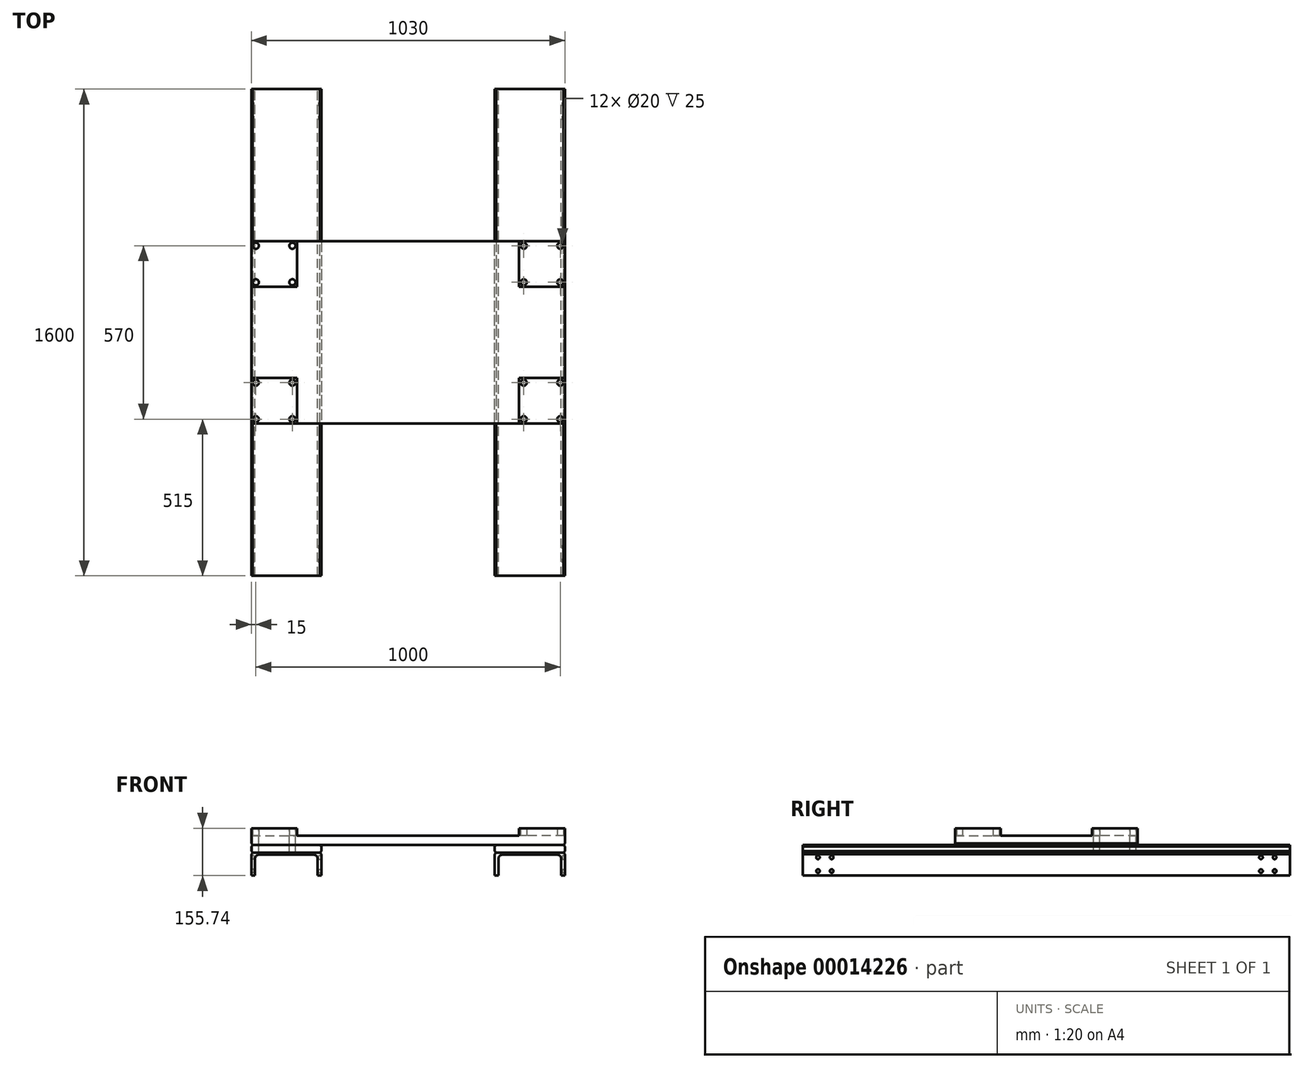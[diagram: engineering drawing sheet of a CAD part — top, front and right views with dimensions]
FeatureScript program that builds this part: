
annotation { "Feature Type Name" : "Feature", "Feature Type Description" : "" }
export const myFeature = defineFeature(function(context is Context, id is Id, definition is map)
    precondition{}
    {
        {
            var Q0;
            Q0=qCreatedBy(makeId("Front.planeOp"),FACE);
            var sketch = newSketch(context, id + "F0", { "sketchPlane" : qUnion([Q0])});
            skLineSegment(sketch, "E0", {"start": v(-285, 0) * mm, "end": v(-285, 75) * mm});
            skLineSegment(sketch, "E1", {"start": v(-285, 75) * mm, "end": v(-400, 75) * mm});
            skLineSegment(sketch, "E2", {"start": v(-285, 0) * mm, "end": v(-297.5, 0) * mm});
            skLineSegment(sketch, "E3", {"start": v(-297.5, 0) * mm, "end": v(-297.5, 56.5) * mm});
            skLineSegment(sketch, "E4", {"start": v(-309.5, 68.5) * mm, "end": v(-400, 68.5) * mm});
            skPoint(sketch, "E5.visualSharp", {"position": v(-297.5, 68.5) * mm});
            skArc(sketch, "E5.filletArc", {"start": v(-297.5, 56.5) * mm, "mid": v(-301.01, 64.99) * mm, "end": v(-309.5, 68.5) * mm});
            skPoint(sketch, "E6.0.MirrorP", {"position": v(-502.5, 68.5) * mm});
            skLineSegment(sketch, "E6.1.MirrorCS", {"start": v(-515, 0) * mm, "end": v(-515, 75) * mm});
            skLineSegment(sketch, "E6.2.MirrorCS", {"start": v(-502.5, 0) * mm, "end": v(-502.5, 56.5) * mm});
            skLineSegment(sketch, "E6.3.MirrorCS", {"start": v(-490.5, 68.5) * mm, "end": v(-400, 68.5) * mm});
            skLineSegment(sketch, "E6.4.MirrorCS", {"start": v(-515, 75) * mm, "end": v(-400, 75) * mm});
            skLineSegment(sketch, "E6.5.MirrorCS", {"start": v(-515, 0) * mm, "end": v(-502.5, 0) * mm});
            skArc(sketch, "E6.6.MirrorCS", {"start": v(-502.5, 56.5) * mm, "mid": v(-498.99, 64.99) * mm, "end": v(-490.5, 68.5) * mm});
            skSolve(sketch);
        }
        {
            var Q0;
            Q0=qSketchRegion(id+"F0",true);
            extrude(context, id + "F1", {"entities" : qUnion([Q0]), "depth" : 1600 * mm});
        }
        {
            var Q0;
            Q0=makeQuery(id+"F1.opExtrude","SWEPT_FACE",FACE,{"disambiguationData":[OSD([sQuery(id+"F0.wireOp",EDGE,"E0")])]});
            var sketch = newSketch(context, id + "F2", { "sketchPlane" : qUnion([Q0])});
            skLineSegment(sketch, "E7", {"start": v(-1600, 37.5) * mm, "end": v(0, 37.5) * mm, "construction": true});
            skLineSegment(sketch, "E8.rect.bottom", {"start": v(-1505, 15) * mm, "end": v(-1550, 15) * mm, "construction": true});
            skLineSegment(sketch, "E8.rect.top", {"start": v(-1505, 60) * mm, "end": v(-1550, 60) * mm, "construction": true});
            skLineSegment(sketch, "E8.rect.left", {"start": v(-1505, 15) * mm, "end": v(-1505, 60) * mm, "construction": true});
            skLineSegment(sketch, "E8.rect.right", {"start": v(-1550, 15) * mm, "end": v(-1550, 60) * mm, "construction": true});
            skPoint(sketch, "E8.rect.middle", {"position": v(-1527.5, 37.5) * mm});
            skCircle(sketch, "E9", {"center": v(-1550, 60) * mm, "radius": 6 * mm});
            skCircle(sketch, "E10", {"center": v(-1505, 60) * mm, "radius": 6 * mm});
            skCircle(sketch, "E11", {"center": v(-1550, 15) * mm, "radius": 6 * mm});
            skCircle(sketch, "E12", {"center": v(-1505, 15) * mm, "radius": 6 * mm});
            skLineSegment(sketch, "E13", {"start": v(-1527.5, 37.5) * mm, "end": v(-1527.5, 75) * mm, "construction": true});
            skLineSegment(sketch, "E14", {"start": v(-1527.5, 75) * mm, "end": v(-1527.5, 0) * mm, "construction": true});
            skLineSegment(sketch, "E15", {"start": v(-800, 75) * mm, "end": v(-800, 0) * mm, "construction": true});
            skLineSegment(sketch, "E16.0.MirrorCS", {"start": v(-72.5, 75) * mm, "end": v(-72.5, 0) * mm, "construction": true});
            skLineSegment(sketch, "E16.1.MirrorCS", {"start": v(-72.5, 37.5) * mm, "end": v(-72.5, 75) * mm, "construction": true});
            skCircle(sketch, "E16.2.MirrorC", {"center": v(-50, 60) * mm, "radius": 6 * mm});
            skCircle(sketch, "E16.3.MirrorC", {"center": v(-95, 60) * mm, "radius": 6 * mm});
            skLineSegment(sketch, "E16.4.MirrorCS", {"start": v(-95, 15) * mm, "end": v(-95, 60) * mm, "construction": true});
            skLineSegment(sketch, "E16.5.MirrorCS", {"start": v(-50, 15) * mm, "end": v(-50, 60) * mm, "construction": true});
            skLineSegment(sketch, "E16.6.MirrorCS", {"start": v(-95, 15) * mm, "end": v(-50, 15) * mm, "construction": true});
            skCircle(sketch, "E16.7.MirrorC", {"center": v(-95, 15) * mm, "radius": 6 * mm});
            skCircle(sketch, "E16.8.MirrorC", {"center": v(-50, 15) * mm, "radius": 6 * mm});
            skLineSegment(sketch, "E16.9.MirrorCS", {"start": v(-95, 60) * mm, "end": v(-50, 60) * mm, "construction": true});
            skPoint(sketch, "E16.10.MirrorP", {"position": v(-72.5, 37.5) * mm});
            skSolve(sketch);
        }
        {
            var Q0;
            Q0=qSketchRegion(id+"F2",true);
            extrude(context, id + "F3", {"entities" : qUnion([Q0]), "oppositeDirection" : true, "depth" : 8 * mm});
        }
        {
            var Q0;
            Q0=makeQuery(id+"F1.opExtrude","SWEPT_FACE",FACE,{"disambiguationData":[OSD([sQuery(id+"F0.wireOp",EDGE,"E6.1.MirrorCS")])]});
            var sketch = newSketch(context, id + "F4", { "sketchPlane" : qUnion([Q0])});
            skLineSegment(sketch, "E17", {"start": v(0, 37.5) * mm, "end": v(1600, 37.5) * mm, "construction": true});
            skLineSegment(sketch, "E18.rect.bottom", {"start": v(95, 15) * mm, "end": v(50, 15) * mm, "construction": true});
            skLineSegment(sketch, "E18.rect.top", {"start": v(95, 60) * mm, "end": v(50, 60) * mm, "construction": true});
            skLineSegment(sketch, "E18.rect.left", {"start": v(95, 15) * mm, "end": v(95, 60) * mm, "construction": true});
            skLineSegment(sketch, "E18.rect.right", {"start": v(50, 15) * mm, "end": v(50, 60) * mm, "construction": true});
            skPoint(sketch, "E18.rect.middle", {"position": v(72.5, 37.5) * mm});
            skCircle(sketch, "E19", {"center": v(50, 60) * mm, "radius": 6 * mm});
            skCircle(sketch, "E20", {"center": v(95, 60) * mm, "radius": 6 * mm});
            skCircle(sketch, "E21", {"center": v(50, 15) * mm, "radius": 6 * mm});
            skCircle(sketch, "E22", {"center": v(95, 15) * mm, "radius": 6 * mm});
            skLineSegment(sketch, "E23", {"start": v(72.5, 37.5) * mm, "end": v(72.5, 75) * mm, "construction": true});
            skLineSegment(sketch, "E24", {"start": v(72.5, 75) * mm, "end": v(72.5, 0) * mm, "construction": true});
            skLineSegment(sketch, "E25", {"start": v(800, 75) * mm, "end": v(800, 0) * mm, "construction": true});
            skLineSegment(sketch, "E26.0.MirrorCS", {"start": v(1527.5, 75) * mm, "end": v(1527.5, 0) * mm, "construction": true});
            skLineSegment(sketch, "E26.1.MirrorCS", {"start": v(1527.5, 37.5) * mm, "end": v(1527.5, 75) * mm, "construction": true});
            skCircle(sketch, "E26.2.MirrorC", {"center": v(1550, 60) * mm, "radius": 6 * mm});
            skCircle(sketch, "E26.3.MirrorC", {"center": v(1505, 60) * mm, "radius": 6 * mm});
            skLineSegment(sketch, "E26.4.MirrorCS", {"start": v(1505, 15) * mm, "end": v(1505, 60) * mm, "construction": true});
            skLineSegment(sketch, "E26.5.MirrorCS", {"start": v(1550, 15) * mm, "end": v(1550, 60) * mm, "construction": true});
            skLineSegment(sketch, "E26.6.MirrorCS", {"start": v(1505, 15) * mm, "end": v(1550, 15) * mm, "construction": true});
            skCircle(sketch, "E26.7.MirrorC", {"center": v(1505, 15) * mm, "radius": 6 * mm});
            skCircle(sketch, "E26.8.MirrorC", {"center": v(1550, 15) * mm, "radius": 6 * mm});
            skLineSegment(sketch, "E26.9.MirrorCS", {"start": v(1505, 60) * mm, "end": v(1550, 60) * mm, "construction": true});
            skPoint(sketch, "E26.10.MirrorP", {"position": v(1527.5, 37.5) * mm});
            skLineSegment(sketch, "E27", {"start": v(0, 75) * mm, "end": v(1600, 0) * mm, "construction": true});
            skLineSegment(sketch, "E28", {"start": v(1600, 0) * mm, "end": v(1600, 75) * mm, "construction": true});
            skLineSegment(sketch, "E29", {"start": v(1600, 75) * mm, "end": v(0, 0) * mm, "construction": true});
            skLineSegment(sketch, "E30", {"start": v(0, 0) * mm, "end": v(0, 75) * mm, "construction": true});
            skPoint(sketch, "E31", {"position": v(800, 37.5) * mm});
            skPoint(sketch, "E32", {"position": v(1600, 37.5) * mm});
            skPoint(sketch, "E33", {"position": v(0, 37.5) * mm});
            skSolve(sketch);
        }
        {
            var Q0;
            Q0=qSketchRegion(id+"F4",true);
            extrude(context, id + "F5", {"entities" : qUnion([Q0]), "operationType" : NewBodyOperationType.REMOVE, "oppositeDirection" : true, "depth" : 8 * mm});
        }
        {
            var Q0;
            Q0=makeQuery(id+"F1.opExtrude","SWEPT_FACE",FACE,{"disambiguationData":[OSD([sQuery(id+"F0.wireOp",EDGE,"E1"),sQuery(id+"F0.wireOp",EDGE,"E6.4.MirrorCS")])]});
            var sketch = newSketch(context, id + "F6", { "sketchPlane" : qUnion([Q0])});
            skLineSegment(sketch, "E34.bottom", {"start": v(-515, 0) * mm, "end": v(-285, 0) * mm});
            skLineSegment(sketch, "E34.top", {"start": v(-515, -1600) * mm, "end": v(-285, -1600) * mm});
            skLineSegment(sketch, "E34.left", {"start": v(-515, 0) * mm, "end": v(-515, -1600) * mm});
            skLineSegment(sketch, "E34.right", {"start": v(-285, 0) * mm, "end": v(-285, -1600) * mm});
            skSolve(sketch);
        }
        {
            var Q0;
            Q0=qSketchRegion(id+"F6",true);
            extrude(context, id + "F7", {"entities" : qUnion([Q0]), "depth" : 25.74 * mm});
        }
        {
            var Q0;
            Q0=makeQuery(id+"F1.opExtrude","SWEPT_BODY",BODY,{"disambiguationData":[OSD([sQuery(id+"F0.wireOp",EDGE,"E0"),sQuery(id+"F0.wireOp",EDGE,"E1"),sQuery(id+"F0.wireOp",EDGE,"E2"),sQuery(id+"F0.wireOp",EDGE,"E3"),sQuery(id+"F0.wireOp",EDGE,"E4"),sQuery(id+"F0.wireOp",EDGE,"E5.filletArc"),sQuery(id+"F0.wireOp",EDGE,"E6.1.MirrorCS"),sQuery(id+"F0.wireOp",EDGE,"E6.2.MirrorCS"),sQuery(id+"F0.wireOp",EDGE,"E6.3.MirrorCS"),sQuery(id+"F0.wireOp",EDGE,"E6.4.MirrorCS"),sQuery(id+"F0.wireOp",EDGE,"E6.5.MirrorCS"),sQuery(id+"F0.wireOp",EDGE,"E6.6.MirrorCS")])]});
            var Q1;
            Q1=makeQuery(id+"F7.opExtrude","SWEPT_BODY",BODY,{"disambiguationData":[OSD([sQuery(id+"F6.wireOp",EDGE,"E34.bottom"),sQuery(id+"F6.wireOp",EDGE,"E34.top"),sQuery(id+"F6.wireOp",EDGE,"E34.left"),sQuery(id+"F6.wireOp",EDGE,"E34.right")])]});
            var Q2;
            Q2=qCreatedBy(makeId("Right.planeOp"),FACE);
            mirror(context, id + "F8", {"entities" : qUnion([Q0, Q1]), "mirrorPlane" : qUnion([Q2])});
        }
        {
            var Q0;
            Q0=makeQuery(id+"F7.opExtrude","CAP_FACE",FACE,{"disambiguationData":[OSD([sQuery(id+"F6.wireOp",EDGE,"E34.bottom"),sQuery(id+"F6.wireOp",EDGE,"E34.top"),sQuery(id+"F6.wireOp",EDGE,"E34.left"),sQuery(id+"F6.wireOp",EDGE,"E34.right")])],"isStart":false});
            var sketch = newSketch(context, id + "F9", { "sketchPlane" : qUnion([Q0])});
            skLineSegment(sketch, "E35", {"start": v(-515, -800) * mm, "end": v(515, -800) * mm, "construction": true});
            skLineSegment(sketch, "E36", {"start": v(-515, -800) * mm, "end": v(-515, -500) * mm});
            skLineSegment(sketch, "E37", {"start": v(-515, -500) * mm, "end": v(515, -500) * mm});
            skLineSegment(sketch, "E38", {"start": v(515, -500) * mm, "end": v(515, -800) * mm});
            skLineSegment(sketch, "E39.0.MirrorCS", {"start": v(-515, -800) * mm, "end": v(-515, -1100) * mm});
            skLineSegment(sketch, "E39.1.MirrorCS", {"start": v(-515, -1100) * mm, "end": v(515, -1100) * mm});
            skLineSegment(sketch, "E39.2.MirrorCS", {"start": v(515, -1100) * mm, "end": v(515, -800) * mm});
            skSolve(sketch);
        }
        {
            var Q0;
            Q0=qSketchRegion(id+"F9",true);
            extrude(context, id + "F10", {"entities" : qUnion([Q0]), "depth" : 30 * mm});
        }
        {
            var Q0;
            Q0=makeQuery(id+"F8.opPattern","COPY",EDGE,{"derivedFrom":makeQuery(id+"F7.opExtrude","CAP_EDGE",EDGE,{"disambiguationData":[OSD([sQuery(id+"F6.wireOp",EDGE,"E34.left")])],"isStart":false}),"instanceName":"1"});
            var Q1;
            Q1=makeQuery(id+"F8.opPattern","COPY",EDGE,{"derivedFrom":makeQuery(id+"F7.opExtrude","CAP_EDGE",EDGE,{"disambiguationData":[OSD([sQuery(id+"F6.wireOp",EDGE,"E34.right")])],"isStart":false}),"instanceName":"1"});
            var Q2;
            Q2=makeQuery(id+"F7.opExtrude","CAP_EDGE",EDGE,{"disambiguationData":[OSD([sQuery(id+"F6.wireOp",EDGE,"E34.right")])],"isStart":false});
            var Q3;
            Q3=makeQuery(id+"F7.opExtrude","CAP_EDGE",EDGE,{"disambiguationData":[OSD([sQuery(id+"F6.wireOp",EDGE,"E34.left")])],"isStart":false});
            var Q4;
            Q4=makeQuery(id+"F1.opExtrude","SWEPT_EDGE",EDGE,{"disambiguationData":[OSD([sQuery(id+"F0.wireOp",EDGE,"E0"),sQuery(id+"F0.wireOp",EDGE,"E1")])]});
            var Q5;
            Q5=makeQuery(id+"F1.opExtrude","SWEPT_EDGE",EDGE,{"disambiguationData":[OSD([sQuery(id+"F0.wireOp",EDGE,"E6.1.MirrorCS"),sQuery(id+"F0.wireOp",EDGE,"E6.4.MirrorCS")])]});
            var Q6;
            Q6=makeQuery(id+"F8.opPattern","COPY",EDGE,{"derivedFrom":makeQuery(id+"F1.opExtrude","SWEPT_EDGE",EDGE,{"disambiguationData":[OSD([sQuery(id+"F0.wireOp",EDGE,"E6.1.MirrorCS"),sQuery(id+"F0.wireOp",EDGE,"E6.4.MirrorCS")])]}),"instanceName":"1"});
            var Q7;
            Q7=makeQuery(id+"F8.opPattern","COPY",EDGE,{"derivedFrom":makeQuery(id+"F1.opExtrude","SWEPT_EDGE",EDGE,{"disambiguationData":[OSD([sQuery(id+"F0.wireOp",EDGE,"E0"),sQuery(id+"F0.wireOp",EDGE,"E1")])]}),"instanceName":"1"});
            chamfer(context, id + "F11", {"entities" : qUnion([Q0, Q1, Q2, Q3, Q4, Q5, Q6, Q7]), "width" : 5 * mm, "tangentPropagation" : true});
        }
        {
            var Q0;
            Q0=makeQuery(id+"F7.opExtrude","CAP_EDGE",EDGE,{"disambiguationData":[OSD([sQuery(id+"F6.wireOp",EDGE,"E34.right")])],"isStart":true});
            var Q1;
            Q1=makeQuery(id+"F7.opExtrude","CAP_EDGE",EDGE,{"disambiguationData":[OSD([sQuery(id+"F6.wireOp",EDGE,"E34.left")])],"isStart":true});
            var Q2;
            Q2=makeQuery(id+"F8.opPattern","COPY",EDGE,{"derivedFrom":makeQuery(id+"F7.opExtrude","CAP_EDGE",EDGE,{"disambiguationData":[OSD([sQuery(id+"F6.wireOp",EDGE,"E34.right")])],"isStart":true}),"instanceName":"1"});
            var Q3;
            Q3=makeQuery(id+"F8.opPattern","COPY",EDGE,{"derivedFrom":makeQuery(id+"F7.opExtrude","CAP_EDGE",EDGE,{"disambiguationData":[OSD([sQuery(id+"F6.wireOp",EDGE,"E34.left")])],"isStart":true}),"instanceName":"1"});
            var Q4;
            Q4=makeQuery(id+"F10.opExtrude","CAP_EDGE",EDGE,{"disambiguationData":[OSD([sQuery(id+"F9.wireOp",EDGE,"E38"),sQuery(id+"F9.wireOp",EDGE,"E39.2.MirrorCS")])],"isStart":true});
            var Q5;
            Q5=makeQuery(id+"F10.opExtrude","CAP_EDGE",EDGE,{"disambiguationData":[OSD([sQuery(id+"F9.wireOp",EDGE,"E36"),sQuery(id+"F9.wireOp",EDGE,"E39.0.MirrorCS")])],"isStart":true});
            chamfer(context, id + "F12", {"entities" : qUnion([Q0, Q1, Q2, Q3, Q4, Q5]), "width" : 5 * mm, "tangentPropagation" : true});
        }
        {
            var Q0;
            Q0=makeQuery(id+"F10.opExtrude","CAP_FACE",FACE,{"disambiguationData":[OSD([sQuery(id+"F9.wireOp",EDGE,"E36"),sQuery(id+"F9.wireOp",EDGE,"E37"),sQuery(id+"F9.wireOp",EDGE,"E38"),sQuery(id+"F9.wireOp",EDGE,"E39.0.MirrorCS"),sQuery(id+"F9.wireOp",EDGE,"E39.1.MirrorCS"),sQuery(id+"F9.wireOp",EDGE,"E39.2.MirrorCS")])],"isStart":false});
            var sketch = newSketch(context, id + "F13", { "sketchPlane" : qUnion([Q0])});
            skLineSegment(sketch, "E40", {"start": v(0, -500) * mm, "end": v(0, -1100) * mm});
            skLineSegment(sketch, "E41", {"start": v(0, -800) * mm, "end": v(-515, -800) * mm});
            skLineSegment(sketch, "E42.rect.bottom", {"start": v(-515, -500) * mm, "end": v(-365, -500) * mm});
            skLineSegment(sketch, "E42.rect.top", {"start": v(-515, -650) * mm, "end": v(-365, -650) * mm});
            skLineSegment(sketch, "E42.rect.left", {"start": v(-515, -500) * mm, "end": v(-515, -650) * mm});
            skLineSegment(sketch, "E42.rect.right", {"start": v(-365, -500) * mm, "end": v(-365, -650) * mm});
            skPoint(sketch, "E42.rect.middle", {"position": v(-440, -575) * mm});
            skCircle(sketch, "E43", {"center": v(-500, -515) * mm, "radius": 10 * mm});
            skCircle(sketch, "E44", {"center": v(-380, -515) * mm, "radius": 10 * mm});
            skCircle(sketch, "E45", {"center": v(-380, -635) * mm, "radius": 10 * mm});
            skCircle(sketch, "E46", {"center": v(-500, -635) * mm, "radius": 10 * mm});
            skLineSegment(sketch, "E47", {"start": v(-440, -575) * mm, "end": v(-440, -500) * mm, "construction": true});
            skLineSegment(sketch, "E48", {"start": v(-440, -500) * mm, "end": v(-440, -650) * mm, "construction": true});
            skLineSegment(sketch, "E49.0.MirrorCS", {"start": v(0, -800) * mm, "end": v(515, -800) * mm});
            skLineSegment(sketch, "E50.0.MirrorCS", {"start": v(-440, -1025) * mm, "end": v(-440, -1100) * mm, "construction": true});
            skCircle(sketch, "E50.3.MirrorC", {"center": v(-380, -1085) * mm, "radius": 10 * mm});
            skCircle(sketch, "E50.4.MirrorC", {"center": v(-500, -1085) * mm, "radius": 10 * mm});
            skCircle(sketch, "E50.6.MirrorC", {"center": v(-500, -965) * mm, "radius": 10 * mm});
            skPoint(sketch, "E50.7.MirrorP", {"position": v(-440, -1025) * mm});
            skLineSegment(sketch, "E50.12.MirrorCS", {"start": v(-440, -1100) * mm, "end": v(-440, -950) * mm, "construction": true});
            skLineSegment(sketch, "E50.16.MirrorCS", {"start": v(-515, -950) * mm, "end": v(-365, -950) * mm});
            skLineSegment(sketch, "E50.17.MirrorCS", {"start": v(-365, -1100) * mm, "end": v(-365, -950) * mm});
            skCircle(sketch, "E50.18.MirrorC", {"center": v(-380, -965) * mm, "radius": 10 * mm});
            skPoint(sketch, "E50.19.MirrorP", {"position": v(-440, -1025) * mm});
            skLineSegment(sketch, "E50.20.MirrorCS", {"start": v(-515, -1100) * mm, "end": v(-365, -1100) * mm});
            skLineSegment(sketch, "E50.23.MirrorCS", {"start": v(-515, -1100) * mm, "end": v(-515, -950) * mm});
            skLineSegment(sketch, "E51.0.MirrorCS", {"start": v(440, -575) * mm, "end": v(440, -500) * mm, "construction": true});
            skCircle(sketch, "E51.1.MirrorC", {"center": v(500, -965) * mm, "radius": 10 * mm});
            skCircle(sketch, "E51.2.MirrorC", {"center": v(500, -635) * mm, "radius": 10 * mm});
            skCircle(sketch, "E51.3.MirrorC", {"center": v(380, -1085) * mm, "radius": 10 * mm});
            skCircle(sketch, "E51.4.MirrorC", {"center": v(380, -965) * mm, "radius": 10 * mm});
            skCircle(sketch, "E51.5.MirrorC", {"center": v(500, -1085) * mm, "radius": 10 * mm});
            skCircle(sketch, "E51.6.MirrorC", {"center": v(380, -515) * mm, "radius": 10 * mm});
            skCircle(sketch, "E51.7.MirrorC", {"center": v(380, -635) * mm, "radius": 10 * mm});
            skCircle(sketch, "E51.8.MirrorC", {"center": v(500, -515) * mm, "radius": 10 * mm});
            skLineSegment(sketch, "E51.9.MirrorCS", {"start": v(515, -1100) * mm, "end": v(365, -1100) * mm});
            skLineSegment(sketch, "E51.10.MirrorCS", {"start": v(440, -500) * mm, "end": v(440, -650) * mm, "construction": true});
            skLineSegment(sketch, "E51.11.MirrorCS", {"start": v(515, -950) * mm, "end": v(365, -950) * mm});
            skPoint(sketch, "E51.12.MirrorP", {"position": v(440, -575) * mm});
            skLineSegment(sketch, "E51.13.MirrorCS", {"start": v(515, -1100) * mm, "end": v(515, -950) * mm});
            skPoint(sketch, "E51.14.MirrorP", {"position": v(440, -1025) * mm});
            skLineSegment(sketch, "E51.15.MirrorCS", {"start": v(515, -500) * mm, "end": v(515, -650) * mm});
            skPoint(sketch, "E51.16.MirrorP", {"position": v(440, -1025) * mm});
            skLineSegment(sketch, "E51.17.MirrorCS", {"start": v(440, -1025) * mm, "end": v(440, -1100) * mm, "construction": true});
            skLineSegment(sketch, "E51.18.MirrorCS", {"start": v(440, -1100) * mm, "end": v(440, -950) * mm, "construction": true});
            skLineSegment(sketch, "E51.19.MirrorCS", {"start": v(515, -650) * mm, "end": v(365, -650) * mm});
            skLineSegment(sketch, "E51.20.MirrorCS", {"start": v(515, -500) * mm, "end": v(365, -500) * mm});
            skLineSegment(sketch, "E51.21.MirrorCS", {"start": v(365, -1100) * mm, "end": v(365, -950) * mm});
            skLineSegment(sketch, "E51.22.MirrorCS", {"start": v(365, -500) * mm, "end": v(365, -650) * mm});
            skPoint(sketch, "E51.23.MirrorP", {"position": v(440, -575) * mm});
            skSolve(sketch);
        }
        {
            var Q0;
            Q0=makeQuery(id+"F13.imprint","IMPRINT",FACE,{"disambiguationData":[TD([[makeQuery(id+"F13.imprint","IMPRINT",EDGE,{"derivedFrom":sQuery(id+"F13.wireOp",EDGE,"E43")}),1.0]])]});
            var Q1;
            Q1=makeQuery(id+"F13.imprint","IMPRINT",FACE,{"disambiguationData":[TD([[makeQuery(id+"F13.imprint","IMPRINT",EDGE,{"derivedFrom":sQuery(id+"F13.wireOp",EDGE,"E44")}),1.0]])]});
            var Q2;
            Q2=makeQuery(id+"F13.imprint","IMPRINT",FACE,{"disambiguationData":[TD([[makeQuery(id+"F13.imprint","IMPRINT",EDGE,{"derivedFrom":sQuery(id+"F13.wireOp",EDGE,"E46")}),1.0]])]});
            var Q3;
            Q3=makeQuery(id+"F13.imprint","IMPRINT",FACE,{"disambiguationData":[TD([[makeQuery(id+"F13.imprint","IMPRINT",EDGE,{"derivedFrom":sQuery(id+"F13.wireOp",EDGE,"E45")}),1.0]])]});
            var Q4;
            Q4=makeQuery(id+"F1.opExtrude","SWEPT_BODY",BODY,{"disambiguationData":[OSD([sQuery(id+"F0.wireOp",EDGE,"E0"),sQuery(id+"F0.wireOp",EDGE,"E1"),sQuery(id+"F0.wireOp",EDGE,"E2"),sQuery(id+"F0.wireOp",EDGE,"E3"),sQuery(id+"F0.wireOp",EDGE,"E4"),sQuery(id+"F0.wireOp",EDGE,"E5.filletArc"),sQuery(id+"F0.wireOp",EDGE,"E6.1.MirrorCS"),sQuery(id+"F0.wireOp",EDGE,"E6.2.MirrorCS"),sQuery(id+"F0.wireOp",EDGE,"E6.3.MirrorCS"),sQuery(id+"F0.wireOp",EDGE,"E6.4.MirrorCS"),sQuery(id+"F0.wireOp",EDGE,"E6.5.MirrorCS"),sQuery(id+"F0.wireOp",EDGE,"E6.6.MirrorCS")])]});
            extrude(context, id + "F14", {"entities" : qUnion([Q0, Q1, Q2, Q3]), "operationType" : NewBodyOperationType.REMOVE, "endBound" : BoundingType.UP_TO_BODY, "oppositeDirection" : true, "endBoundEntityBody" : qUnion([Q4]), "depth" : 25 * mm});
        }
        {
            var Q0;
            Q0=qSketchRegion(id+"F13",true);
            extrude(context, id + "F15", {"entities" : qUnion([Q0]), "operationType" : NewBodyOperationType.ADD, "depth" : 25 * mm});
        }
        {
            var Q0;
            Q0=makeQuery(id+"F13.imprint","IMPRINT",FACE,{"disambiguationData":[TD([[makeQuery(id+"F13.imprint","IMPRINT",EDGE,{"derivedFrom":sQuery(id+"F13.wireOp",EDGE,"E43")}),1.0]])]});
            var Q1;
            Q1=makeQuery(id+"F13.imprint","IMPRINT",FACE,{"disambiguationData":[TD([[makeQuery(id+"F13.imprint","IMPRINT",EDGE,{"derivedFrom":sQuery(id+"F13.wireOp",EDGE,"E46")}),1.0]])]});
            var Q2;
            Q2=makeQuery(id+"F13.imprint","IMPRINT",FACE,{"disambiguationData":[TD([[makeQuery(id+"F13.imprint","IMPRINT",EDGE,{"derivedFrom":sQuery(id+"F13.wireOp",EDGE,"E45")}),1.0]])]});
            var Q3;
            Q3=makeQuery(id+"F13.imprint","IMPRINT",FACE,{"disambiguationData":[TD([[makeQuery(id+"F13.imprint","IMPRINT",EDGE,{"derivedFrom":sQuery(id+"F13.wireOp",EDGE,"E44")}),1.0]])]});
            var Q4;
            Q4=makeQuery(id+"F7.opExtrude","CAP_FACE",FACE,{"disambiguationData":[OSD([sQuery(id+"F6.wireOp",EDGE,"E34.bottom"),sQuery(id+"F6.wireOp",EDGE,"E34.top"),sQuery(id+"F6.wireOp",EDGE,"E34.left"),sQuery(id+"F6.wireOp",EDGE,"E34.right")])],"isStart":true});
            extrude(context, id + "F16", {"entities" : qUnion([Q0, Q1, Q2, Q3]), "operationType" : NewBodyOperationType.REMOVE, "endBound" : BoundingType.UP_TO_SURFACE, "oppositeDirection" : true, "endBoundEntityFace" : qUnion([Q4]), "depth" : 4.55 * mm});
        }
    });
